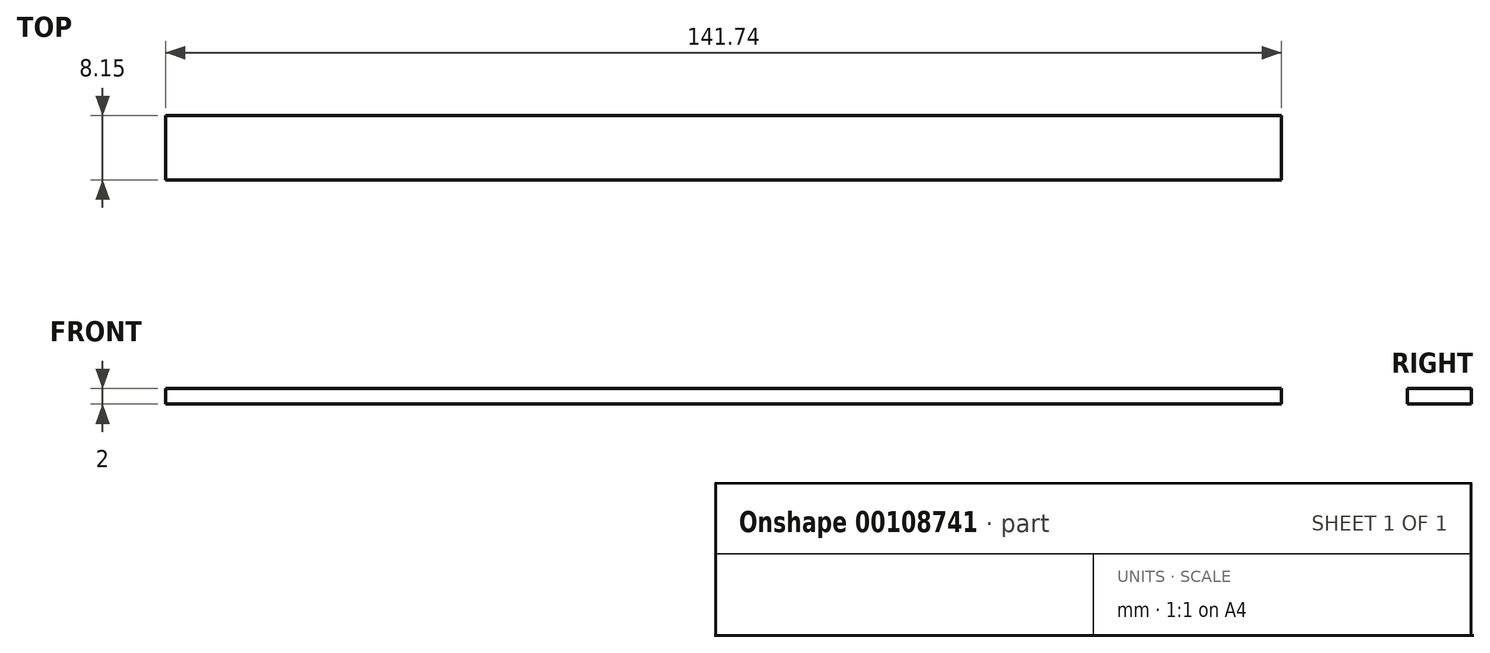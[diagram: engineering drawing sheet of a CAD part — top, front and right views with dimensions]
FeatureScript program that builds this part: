
annotation { "Feature Type Name" : "Feature", "Feature Type Description" : "" }
export const myFeature = defineFeature(function(context is Context, id is Id, definition is map)
    precondition{}
    {
        {
            var Q0;
            Q0=qCreatedBy(makeId("Top.planeOp"),FACE);
            var sketch = newSketch(context, id + "F0", { "sketchPlane" : qUnion([Q0])});
            skLineSegment(sketch, "E0.bottom", {"start": v(-72.18, 3.44) * mm, "end": v(69.56, 3.44) * mm});
            skLineSegment(sketch, "E0.top", {"start": v(-72.18, -4.7) * mm, "end": v(69.56, -4.7) * mm});
            skLineSegment(sketch, "E0.left", {"start": v(-72.18, 3.44) * mm, "end": v(-72.18, -4.7) * mm});
            skLineSegment(sketch, "E0.right", {"start": v(69.56, 3.44) * mm, "end": v(69.56, -4.7) * mm});
            skSolve(sketch);
        }
        {
            var Q0;
            Q0=makeQuery(id+"F0.imprint","IMPRINT",FACE,{"disambiguationData":[TD([[makeQuery(id+"F0.imprint","IMPRINT",EDGE,{"derivedFrom":sQuery(id+"F0.wireOp",EDGE,"E0.bottom")}),-1.0]])]});
            extrude(context, id + "F1", {"entities" : qUnion([Q0]), "depth" : 2 * mm});
        }
    });
